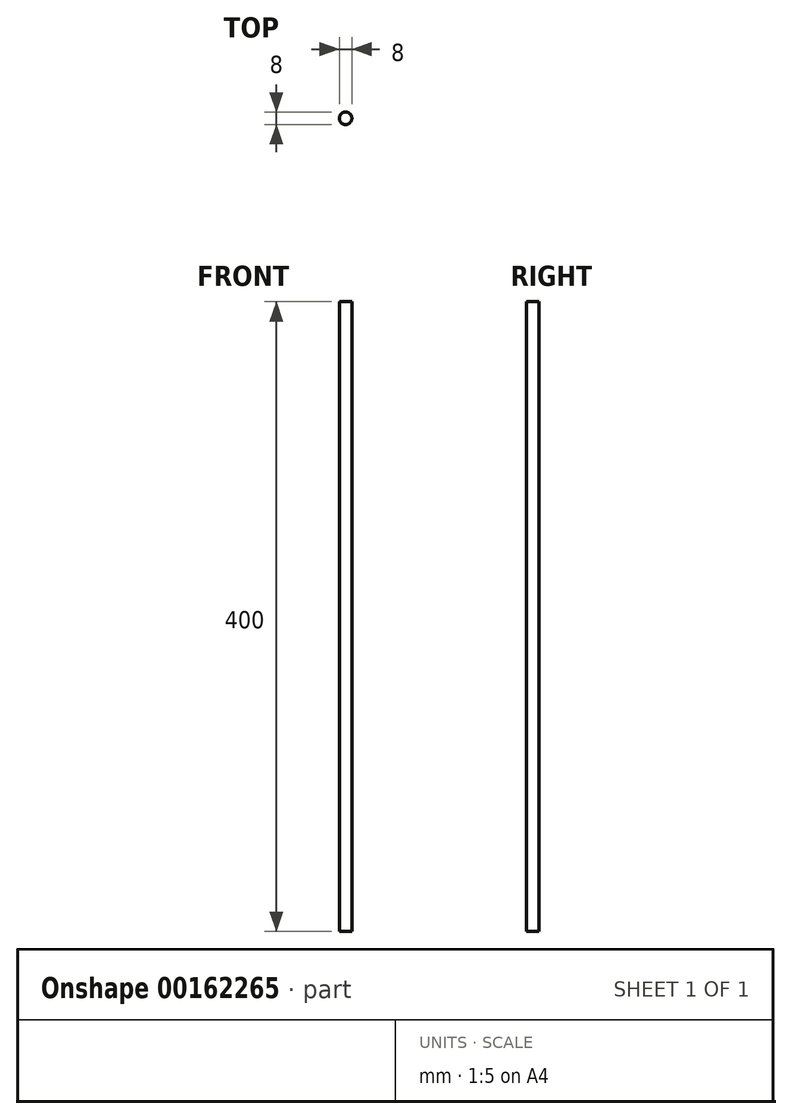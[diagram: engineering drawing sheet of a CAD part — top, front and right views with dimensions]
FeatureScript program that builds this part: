
annotation { "Feature Type Name" : "Feature", "Feature Type Description" : "" }
export const myFeature = defineFeature(function(context is Context, id is Id, definition is map)
    precondition{}
    {
        {
            var Q0;
            Q0=qCreatedBy(makeId("Top.planeOp"),FACE);
            var sketch = newSketch(context, id + "F0", { "sketchPlane" : qUnion([Q0])});
            skCircle(sketch, "E0", {"center": v(0, 0) * mm, "radius": 4 * mm});
            skSolve(sketch);
        }
        {
            var Q0;
            Q0 = qSketchRegion(id + "F0", true);
            extrude(context, id + "F1", {"entities" : qUnion([Q0]), "depth" : 400 * mm});
        }
    });
